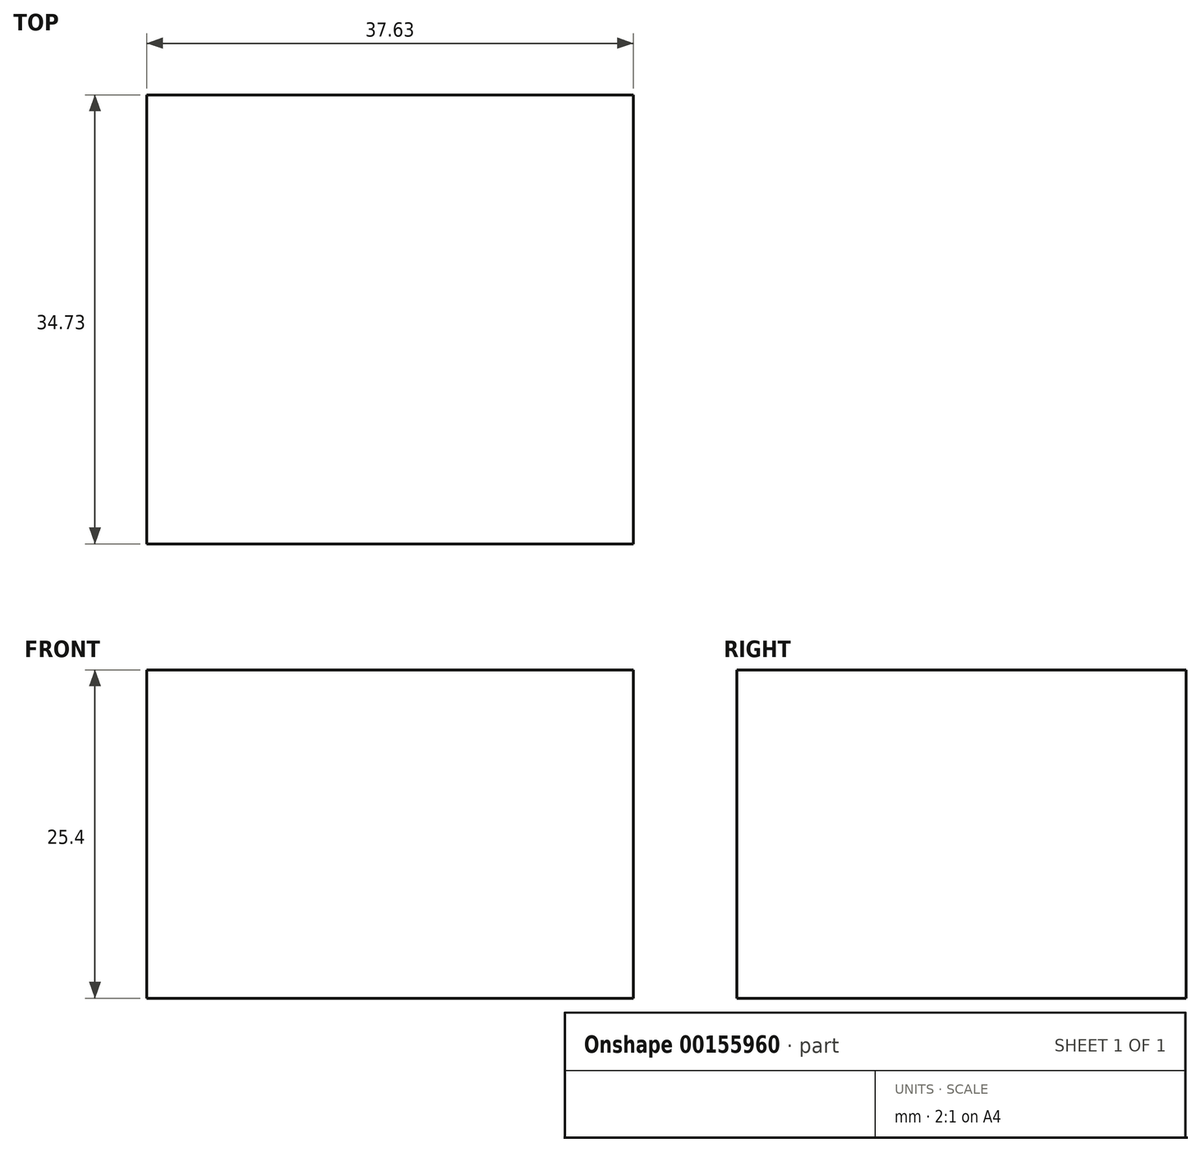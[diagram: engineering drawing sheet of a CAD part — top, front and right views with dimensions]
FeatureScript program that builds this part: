
annotation { "Feature Type Name" : "Feature", "Feature Type Description" : "" }
export const myFeature = defineFeature(function(context is Context, id is Id, definition is map)
    precondition{}
    {
        {
            var Q0;
            Q0=qCreatedBy(makeId("Top.planeOp"),FACE);
            var sketch = newSketch(context, id + "F0", { "sketchPlane" : qUnion([Q0])});
            skLineSegment(sketch, "E0.bottom", {"start": v(-12.07, 0) * mm, "end": v(25.56, 0) * mm});
            skLineSegment(sketch, "E0.top", {"start": v(-12.07, 34.73) * mm, "end": v(25.56, 34.73) * mm});
            skLineSegment(sketch, "E0.left", {"start": v(-12.07, 0) * mm, "end": v(-12.07, 34.73) * mm});
            skLineSegment(sketch, "E0.right", {"start": v(25.56, 0) * mm, "end": v(25.56, 34.73) * mm});
            skSolve(sketch);
        }
        {
            var Q0;
            Q0=makeQuery(id+"F0.imprint","IMPRINT",FACE,{"disambiguationData":[TD([[makeQuery(id+"F0.imprint","IMPRINT",EDGE,{"derivedFrom":sQuery(id+"F0.wireOp",EDGE,"E0.bottom")}),1.0]])]});
            extrude(context, id + "F1", {"entities" : qUnion([Q0]), "depth" : 25.4 * mm});
        }
    });
